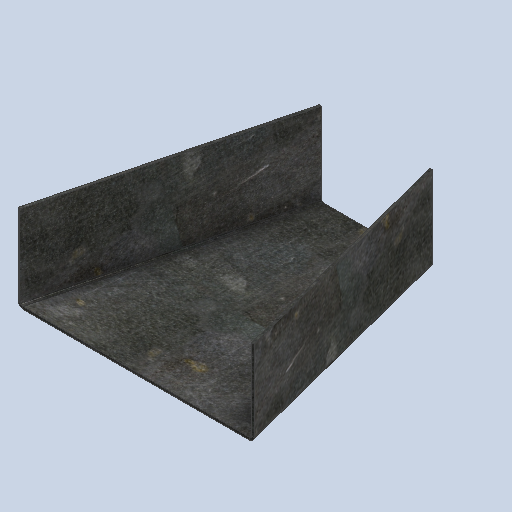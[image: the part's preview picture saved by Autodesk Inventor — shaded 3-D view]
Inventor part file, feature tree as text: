
AUTODESK INVENTOR PART (.ipt)
format: ipt  version: 2024.3 (Build 283343000, 343)  size: 316,928 bytes
history: native  units: mm
features: sheet_metal_op x7, other x4, sketch x3
ambient origin geometry x8: Origin, YZ Plane, XZ Plane, XY Plane, X Axis, Y Axis, Z Axis, Center Point
bodies: Solid1 (feature_tree)
feature tree (14):
  sheet_metal_op  "Face1"
  sheet_metal_op  "Flange1"
  sheet_metal_op  "Flange2"
  sketch  "Sketch1"  dims[d0=200.0mm]
  other  "Plate1"
  sketch  "Sketch2"  dims[d1=197.0mm]
  other  "Plate2"
  sheet_metal_op  "Bend1"
  sheet_metal_op  "Corner1"
  sketch  "Sketch3"  dims[d2=51.5mm d3=51.5mm d4=2.0mm d5=2.0mm d6=1.0mm d7=4.0mm d8=2.0mm d9=71.5mm d10=90.0deg d11=2.0mm d12=8.0mm d13=2.0mm d14=2.0mm d15=2.0mm d16=1.0mm d17=4.0mm d18=2.0mm d19=71.5mm d20=90.0deg d21=2.0mm d22=8.0mm d23=2.0mm d24=2.0mm]
  other  "Plate3"
  sheet_metal_op  "Bend2"
  sheet_metal_op  "Corner2"
  other  "Definition1"
